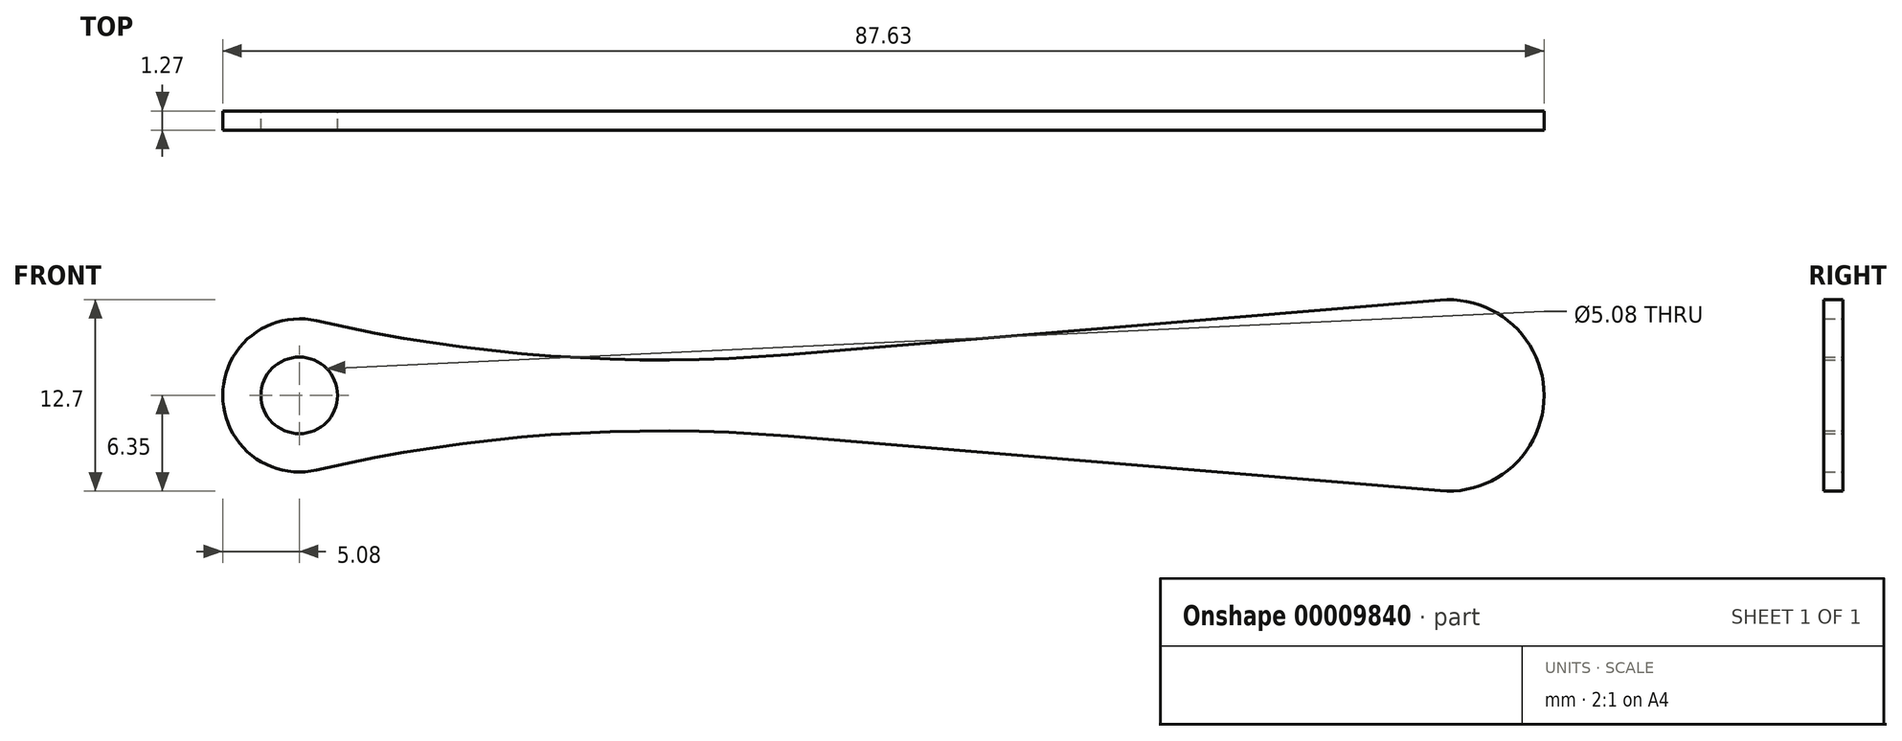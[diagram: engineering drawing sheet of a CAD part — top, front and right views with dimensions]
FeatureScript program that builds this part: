
annotation { "Feature Type Name" : "Feature", "Feature Type Description" : "" }
export const myFeature = defineFeature(function(context is Context, id is Id, definition is map)
    precondition{}
    {
        {
            var Q0;
            Q0=qCreatedBy(makeId("Front.planeOp"),FACE);
            var sketch = newSketch(context, id + "F0", { "sketchPlane" : qUnion([Q0])});
            skArc(sketch, "E0", {"start": v(5.06, 0.42) * mm, "mid": v(-5.08, 0) * mm, "end": v(5.06, -0.42) * mm});
            skArc(sketch, "E1", {"start": v(75.67, -6.33) * mm, "mid": v(82.55, 0) * mm, "end": v(75.67, 6.33) * mm});
            skLineSegment(sketch, "E2", {"start": v(5.06, 0.42) * mm, "end": v(75.67, 6.33) * mm});
            skLineSegment(sketch, "E3", {"start": v(5.06, -0.42) * mm, "end": v(75.67, -6.33) * mm});
            skLineSegment(sketch, "E4", {"start": v(0, 0) * mm, "end": v(76.2, 0) * mm, "construction": true});
            skCircle(sketch, "E5", {"center": v(0, 0) * mm, "radius": 2.54 * mm});
            skSolve(sketch);
        }
        {
            var Q0;
            {var subQ3=sQuery(id+"F0.wireOp",EDGE,"E2");var subQ5=sQuery(id+"F0.wireOp",EDGE,"E0");var subQ7=makeQuery(id+"F0.imprint","INTERSECT",VERTEX,{"derivedFrom":[subQ5,subQ3]});Q0=makeQuery(id+"F0.imprint","IMPRINT",FACE,{"disambiguationData":[TD([[makeQuery(id+"F0.imprint","IMPRINT",EDGE,{"disambiguationData":[TD([[subQ7,-1.0]])],"derivedFrom":subQ5}),1.0]])]});}
            var Q1;
            {var subQ1=sQuery(id+"F0.wireOp",EDGE,"E0");var subQ5=sQuery(id+"F0.wireOp",EDGE,"E2");var subQ6=makeQuery(id+"F0.imprint","INTERSECT",VERTEX,{"derivedFrom":[subQ1,subQ5]});Q1=makeQuery(id+"F0.imprint","IMPRINT",FACE,{"disambiguationData":[TD([[makeQuery(id+"F0.imprint","IMPRINT",EDGE,{"disambiguationData":[TD([[subQ6,1.0]])],"derivedFrom":subQ1}),-1.0]])]});}
            var Q2;
            {var subQ3=sQuery(id+"F0.wireOp",EDGE,"E2");var subQ5=sQuery(id+"F0.wireOp",EDGE,"E0");var subQ7=makeQuery(id+"F0.imprint","INTERSECT",VERTEX,{"derivedFrom":[subQ5,subQ3]});Q2=makeQuery(id+"F0.imprint","IMPRINT",FACE,{"disambiguationData":[TD([[makeQuery(id+"F0.imprint","IMPRINT",EDGE,{"disambiguationData":[TD([[subQ7,1.0]])],"derivedFrom":subQ5}),1.0]])]});}
            var Q3;
            {var subQ0=sQuery(id+"F0.wireOp",EDGE,"E1");var subQ2=makeQuery(id+"F0.imprint","INTERSECT",VERTEX,{"derivedFrom":[subQ0,sQuery(id+"F0.wireOp",EDGE,"E2")]});Q3=makeQuery(id+"F0.imprint","IMPRINT",FACE,{"disambiguationData":[TD([[makeQuery(id+"F0.imprint","IMPRINT",EDGE,{"disambiguationData":[TD([[subQ2,-1.0]])],"derivedFrom":subQ0}),1.0]])]});}
            extrude(context, id + "F1", {"entities" : qUnion([Q0, Q1, Q2, Q3]), "depth" : 1.27 * mm});
        }
        {
            var Q0;
            Q0=makeQuery(id+"F1.opExtrude","SWEPT_EDGE",EDGE,{"disambiguationData":[OSD([sQuery(id+"F0.wireOp",EDGE,"E0"),sQuery(id+"F0.wireOp",EDGE,"E2")])]});
            var Q1;
            Q1=makeQuery(id+"F1.opExtrude","SWEPT_EDGE",EDGE,{"disambiguationData":[OSD([sQuery(id+"F0.wireOp",EDGE,"E0"),sQuery(id+"F0.wireOp",EDGE,"E3")])]});
            fillet(context, id + "F2", {"entities" : qUnion([Q0, Q1]), "radius" : 101.6 * mm, "tangentPropagation" : true, "allowEdgeOverflow" : false});
        }
    });
